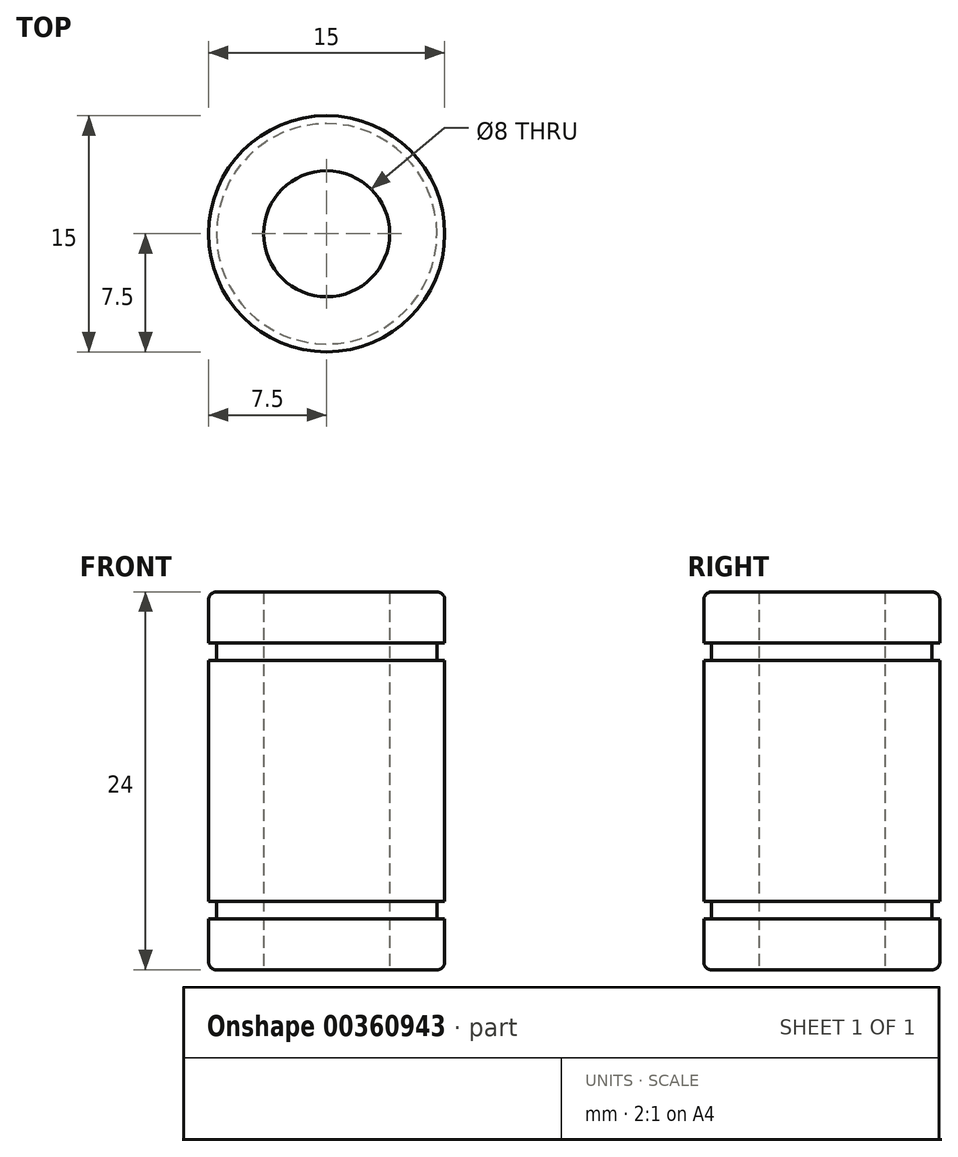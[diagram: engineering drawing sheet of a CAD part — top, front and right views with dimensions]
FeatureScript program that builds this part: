
annotation { "Feature Type Name" : "Feature", "Feature Type Description" : "" }
export const myFeature = defineFeature(function(context is Context, id is Id, definition is map)
    precondition{}
    {
        {
            var Q0;
            Q0=qCreatedBy(makeId("Top.planeOp"),FACE);
            var sketch = newSketch(context, id + "F0", { "sketchPlane" : qUnion([Q0])});
            skCircle(sketch, "E0", {"center": v(0, 0) * mm, "radius": 7.5 * mm});
            skCircle(sketch, "E1", {"center": v(0, 0) * mm, "radius": 4 * mm});
            skSolve(sketch);
        }
        {
            var Q0;
            Q0 = qSketchRegion(id + "F0", true);
            extrude(context, id + "F1", {"entities" : qUnion([Q0]), "depth" : 24 * mm});
        }
        {
            var Q0;
            Q0=makeQuery(id+"F1.opExtrude","CAP_FACE",FACE,{"disambiguationData":[OSD([sQuery(id+"F0.wireOp",EDGE,"E0"),sQuery(id+"F0.wireOp",EDGE,"E1")])],"isStart":false});
            cPlane(context, id + "F2", {"entities" : qUnion([Q0]), "cplaneType" : CPlaneType.OFFSET, "offset" : 3.25 * mm, "oppositeDirection" : true, "width" : 150 * mm, "height" : 150 * mm});
        }
        {
            var Q0;
            Q0=makeQuery(id+"F1.opExtrude","CAP_FACE",FACE,{"disambiguationData":[OSD([sQuery(id+"F0.wireOp",EDGE,"E0"),sQuery(id+"F0.wireOp",EDGE,"E1")])],"isStart":true});
            cPlane(context, id + "F3", {"entities" : qUnion([Q0]), "cplaneType" : CPlaneType.OFFSET, "offset" : 3.25 * mm, "oppositeDirection" : true, "width" : 150 * mm, "height" : 150 * mm});
        }
        {
            var Q0;
            Q0=qCreatedBy(id+"F3.planeOp",FACE);
            var sketch = newSketch(context, id + "F4", { "sketchPlane" : qUnion([Q0])});
            skCircle(sketch, "E2", {"center": v(0, 0) * mm, "radius": 7 * mm});
            skCircle(sketch, "E3", {"center": v(0, 0) * mm, "radius": 7.5 * mm});
            skSolve(sketch);
        }
        {
            var Q0;
            Q0 = qSketchRegion(id + "F4", true);
            extrude(context, id + "F5", {"entities" : qUnion([Q0]), "operationType" : NewBodyOperationType.REMOVE, "oppositeDirection" : true, "depth" : 1.1 * mm});
        }
        {
            var Q0;
            Q0=qCreatedBy(id+"F2.planeOp",FACE);
            var sketch = newSketch(context, id + "F6", { "sketchPlane" : qUnion([Q0])});
            skCircle(sketch, "E4", {"center": v(0, 0) * mm, "radius": 7 * mm});
            skCircle(sketch, "E5", {"center": v(0, 0) * mm, "radius": 7.5 * mm});
            skSolve(sketch);
        }
        {
            var Q0;
            Q0 = qSketchRegion(id + "F6", true);
            extrude(context, id + "F7", {"entities" : qUnion([Q0]), "operationType" : NewBodyOperationType.REMOVE, "oppositeDirection" : true, "depth" : 1.1 * mm});
        }
        {
            var Q0;
            Q0=makeQuery(id+"F1.opExtrude","CAP_EDGE",EDGE,{"disambiguationData":[OSD([sQuery(id+"F0.wireOp",EDGE,"E0")])],"isStart":false});
            var Q1;
            Q1=makeQuery(id+"F1.opExtrude","CAP_EDGE",EDGE,{"disambiguationData":[OSD([sQuery(id+"F0.wireOp",EDGE,"E0")])],"isStart":true});
            fillet(context, id + "F8", {"entities" : qUnion([Q0, Q1]), "radius" : 0.5 * mm, "tangentPropagation" : true, "allowEdgeOverflow" : false});
        }
    });
